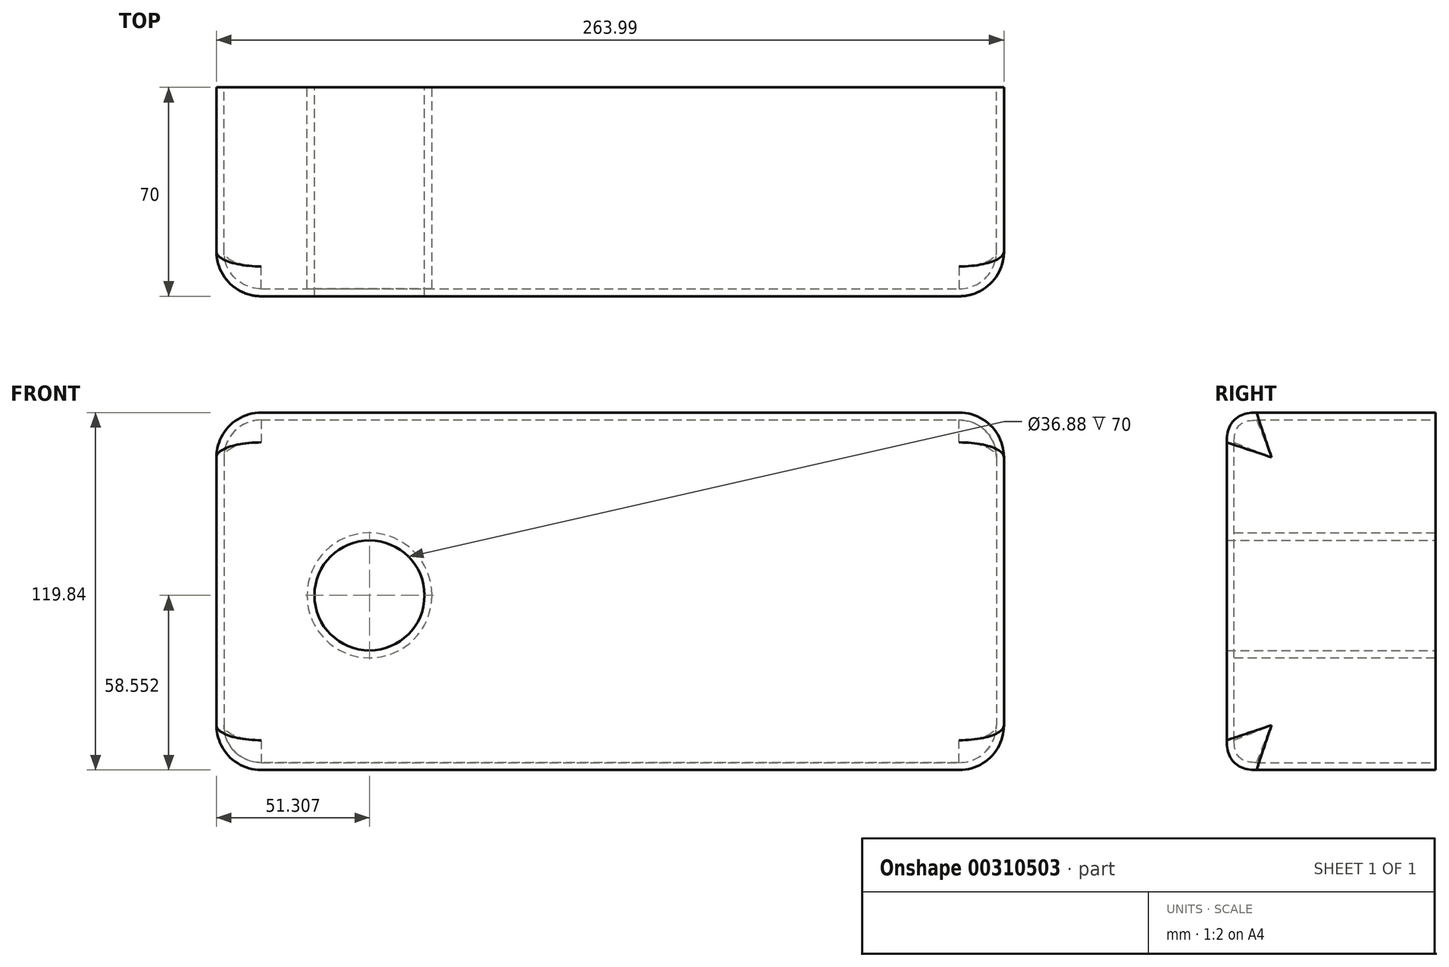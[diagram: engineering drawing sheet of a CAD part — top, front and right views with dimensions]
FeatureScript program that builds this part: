
annotation { "Feature Type Name" : "Feature", "Feature Type Description" : "" }
export const myFeature = defineFeature(function(context is Context, id is Id, definition is map)
    precondition{}
    {
        {
            var Q0;
            Q0=qCreatedBy(makeId("Front.planeOp"),FACE);
            var sketch = newSketch(context, id + "F0", { "sketchPlane" : qUnion([Q0])});
            skLineSegment(sketch, "E0.bottom", {"start": v(-139.46, 68.5) * mm, "end": v(124.53, 68.5) * mm});
            skLineSegment(sketch, "E0.top", {"start": v(-139.46, -51.35) * mm, "end": v(124.53, -51.35) * mm});
            skLineSegment(sketch, "E0.left", {"start": v(-139.46, 68.5) * mm, "end": v(-139.46, -51.35) * mm});
            skLineSegment(sketch, "E0.right", {"start": v(124.53, 68.5) * mm, "end": v(124.53, -51.35) * mm});
            skCircle(sketch, "E1", {"center": v(-88.15, 7.2) * mm, "radius": 18.44 * mm});
            skSolve(sketch);
        }
        {
            var Q0;
            Q0=makeQuery(id+"F0.imprint","IMPRINT",FACE,{"disambiguationData":[TD([[makeQuery(id+"F0.imprint","IMPRINT",EDGE,{"derivedFrom":sQuery(id+"F0.wireOp",EDGE,"E0.bottom")}),-1.0]])]});
            extrude(context, id + "F1", {"entities" : qUnion([Q0]), "depth" : 70 * mm});
        }
        {
            var Q0;
            Q0=makeQuery(id+"F1.opExtrude","CAP_EDGE",EDGE,{"disambiguationData":[OSD([sQuery(id+"F0.wireOp",EDGE,"E0.bottom")])],"isStart":false});
            var Q1;
            Q1=makeQuery(id+"F1.opExtrude","CAP_EDGE",EDGE,{"disambiguationData":[OSD([sQuery(id+"F0.wireOp",EDGE,"E0.top")])],"isStart":false});
            fillet(context, id + "F2", {"entities" : qUnion([Q0, Q1]), "radius" : 10 * mm, "tangentPropagation" : true, "rho" : 0.5, "crossSection" : FilletCrossSection.CONIC, "allowEdgeOverflow" : false});
        }
        {
            var Q0;
            Q0=makeQuery(id+"F1.opExtrude","SWEPT_EDGE",EDGE,{"disambiguationData":[OSD([sQuery(id+"F0.wireOp",EDGE,"E0.top"),sQuery(id+"F0.wireOp",EDGE,"E0.left")])]});
            var Q1;
            Q1=makeQuery(id+"F1.opExtrude","SWEPT_EDGE",EDGE,{"disambiguationData":[OSD([sQuery(id+"F0.wireOp",EDGE,"E0.top"),sQuery(id+"F0.wireOp",EDGE,"E0.right")])]});
            fillet(context, id + "F3", {"entities" : qUnion([Q0, Q1]), "radius" : 15 * mm, "tangentPropagation" : true, "allowEdgeOverflow" : false});
        }
        {
            var Q0;
            Q0=makeQuery(id+"F1.opExtrude","CAP_FACE",FACE,{"disambiguationData":[OSD([sQuery(id+"F0.wireOp",EDGE,"E0.bottom"),sQuery(id+"F0.wireOp",EDGE,"E0.top"),sQuery(id+"F0.wireOp",EDGE,"E0.left"),sQuery(id+"F0.wireOp",EDGE,"E0.right"),sQuery(id+"F0.wireOp",EDGE,"E1")])],"isStart":true});
            shell(context, id + "F4", {"entities" : qUnion([Q0]), "thickness" : 2.5 * mm});
        }
    });
